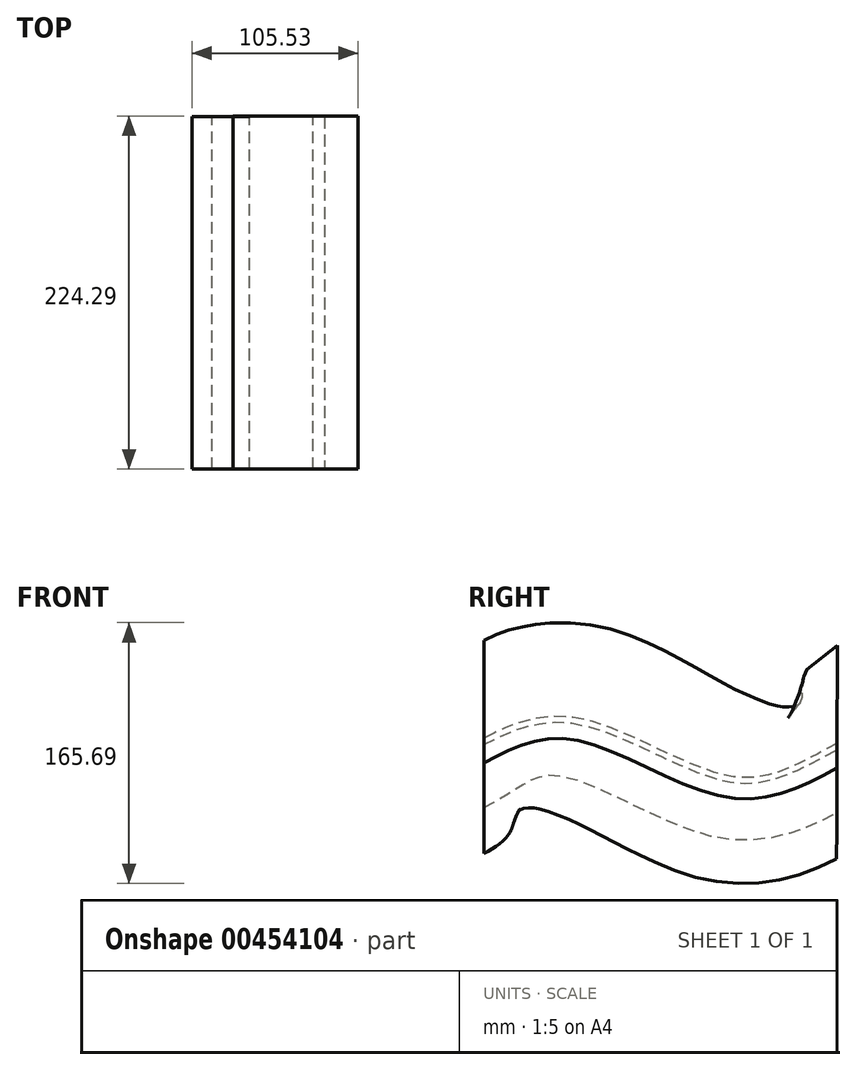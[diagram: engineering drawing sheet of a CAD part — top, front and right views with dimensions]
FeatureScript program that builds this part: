
annotation { "Feature Type Name" : "Feature", "Feature Type Description" : "" }
export const myFeature = defineFeature(function(context is Context, id is Id, definition is map)
    precondition{}
    {
        {
            var Q0;
            Q0=qCreatedBy(makeId("Front.planeOp"),FACE);
            var sketch = newSketch(context, id + "F0", { "sketchPlane" : qUnion([Q0])});
            skArc(sketch, "E0", {"start": v(0, 0) * mm, "mid": v(-0.16, 76.29) * mm, "end": v(-40.47, 11.52) * mm});
            skArc(sketch, "E1", {"start": v(-40.47, 11.52) * mm, "mid": v(-73.63, 4.2) * mm, "end": v(-64.09, -28.39) * mm});
            skArc(sketch, "E2", {"start": v(-64.09, -28.39) * mm, "mid": v(-14.17, -54.55) * mm, "end": v(0, 0) * mm});
            skSolve(sketch);
        }
        {
            var Q0;
            Q0=qCreatedBy(makeId("Right.planeOp"),FACE);
            var sketch = newSketch(context, id + "F1", { "sketchPlane" : qUnion([Q0])});
            skFitSpline(sketch, "E3", {"points": [v(0, 0) * mm, v(55.73, 14.73) * mm, v(155.23, -22.17) * mm, v(224.03, -3.4) * mm], "startDerivative": vector(176.73, 94.27) * mm, "endDerivative": vector(200.55, 106.13) * mm});
            skSolve(sketch);
        }
        {
            var Q0;
            Q0=makeQuery(id+"F0.imprint","IMPRINT",FACE,{"disambiguationData":[TD([[makeQuery(id+"F0.imprint","IMPRINT",EDGE,{"derivedFrom":sQuery(id+"F0.wireOp",EDGE,"E0")}),1.0]])]});
            var Q1;
            Q1=sQuery(id+"F1.wireOp",EDGE,"E3");
            sweep(context, id + "F2", {"profiles" : qUnion([Q0]), "path" : qUnion([Q1])});
        }
    });
